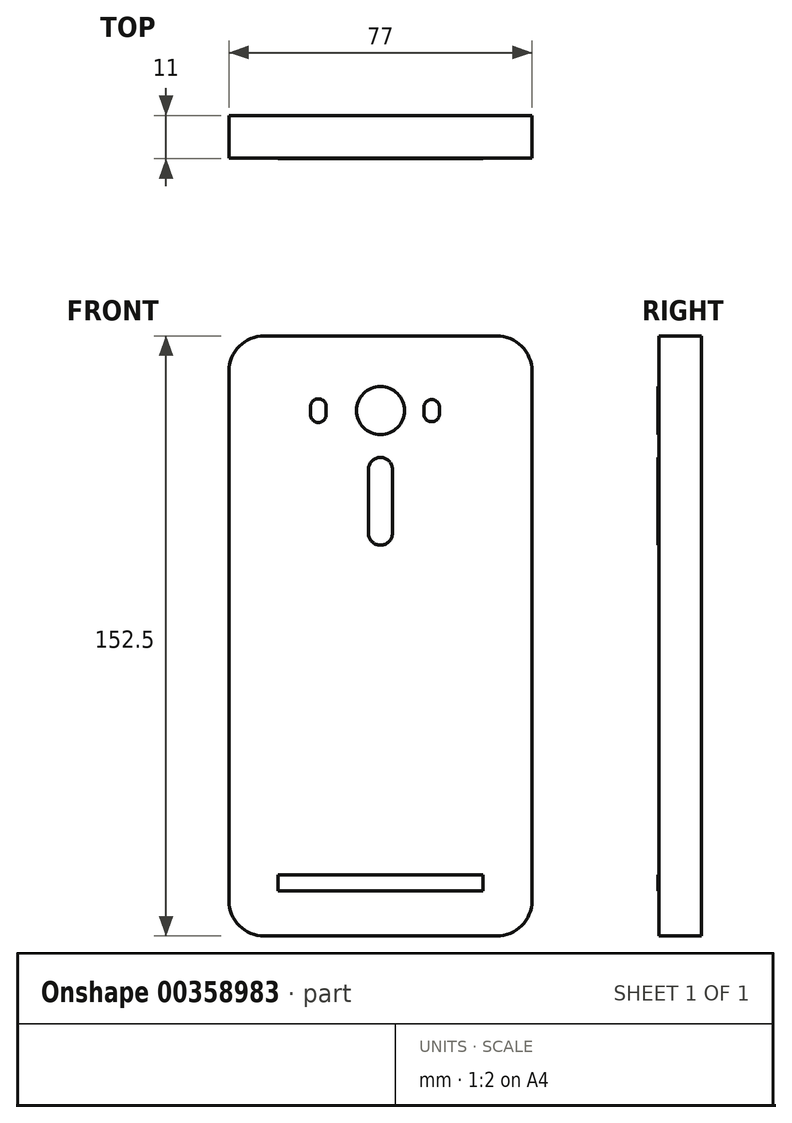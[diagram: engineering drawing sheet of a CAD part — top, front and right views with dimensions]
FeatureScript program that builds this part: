
annotation { "Feature Type Name" : "Feature", "Feature Type Description" : "" }
export const myFeature = defineFeature(function(context is Context, id is Id, definition is map)
    precondition{}
    {
        {
            var Q0;
            Q0=qCreatedBy(makeId("Front.planeOp"),FACE);
            var sketch = newSketch(context, id + "F0", { "sketchPlane" : qUnion([Q0])});
            skLineSegment(sketch, "E0.bottom", {"start": v(29.5, -76.25) * mm, "end": v(-29.5, -76.25) * mm});
            skLineSegment(sketch, "E0.top", {"start": v(29.5, 76.25) * mm, "end": v(-29.5, 76.25) * mm});
            skLineSegment(sketch, "E0.left", {"start": v(38.5, -67.25) * mm, "end": v(38.5, 67.25) * mm});
            skLineSegment(sketch, "E0.right", {"start": v(-38.5, -67.25) * mm, "end": v(-38.5, 67.25) * mm});
            skPoint(sketch, "E0.middle", {"position": v(0, 0) * mm});
            skCircle(sketch, "E1", {"center": v(0, 57.25) * mm, "radius": 6.1 * mm});
            skLineSegment(sketch, "E2.bottom", {"start": v(-15.79, 54.25) * mm, "end": v(-15.79, 54.25) * mm});
            skLineSegment(sketch, "E2.top", {"start": v(-15.79, 60.25) * mm, "end": v(-15.79, 60.25) * mm});
            skLineSegment(sketch, "E2.left", {"start": v(-13.79, 56.25) * mm, "end": v(-13.79, 58.25) * mm});
            skLineSegment(sketch, "E2.right", {"start": v(-17.79, 56.25) * mm, "end": v(-17.79, 58.25) * mm});
            skPoint(sketch, "E2.middle", {"position": v(-15.79, 57.25) * mm});
            skLineSegment(sketch, "E3.bottom", {"start": v(13.01, 54.45) * mm, "end": v(13.01, 54.45) * mm});
            skLineSegment(sketch, "E3.top", {"start": v(13.01, 60.05) * mm, "end": v(13.01, 60.05) * mm});
            skLineSegment(sketch, "E3.left", {"start": v(15.01, 56.45) * mm, "end": v(15.01, 58.05) * mm});
            skLineSegment(sketch, "E3.right", {"start": v(11.01, 56.45) * mm, "end": v(11.01, 58.05) * mm});
            skPoint(sketch, "E3.middle", {"position": v(13.01, 57.25) * mm});
            skLineSegment(sketch, "E4.bottom", {"start": v(0, 23.05) * mm, "end": v(0, 23.05) * mm});
            skLineSegment(sketch, "E4.top", {"start": v(0, 45.35) * mm, "end": v(0, 45.35) * mm});
            skLineSegment(sketch, "E4.left", {"start": v(3.05, 26.1) * mm, "end": v(3.05, 42.3) * mm});
            skLineSegment(sketch, "E4.right", {"start": v(-3.05, 26.1) * mm, "end": v(-3.05, 42.3) * mm});
            skPoint(sketch, "E4.middle", {"position": v(0, 34.2) * mm});
            skPoint(sketch, "E5.visualSharp", {"position": v(-3.05, 45.35) * mm});
            skArc(sketch, "E5.filletArc", {"start": v(0, 45.35) * mm, "mid": v(-2.16, 44.46) * mm, "end": v(-3.05, 42.3) * mm});
            skPoint(sketch, "E6.visualSharp", {"position": v(3.05, 45.35) * mm});
            skArc(sketch, "E6.filletArc", {"start": v(3.05, 42.3) * mm, "mid": v(2.16, 44.46) * mm, "end": v(0, 45.35) * mm});
            skPoint(sketch, "E7.visualSharp", {"position": v(-3.05, 23.05) * mm});
            skArc(sketch, "E7.filletArc", {"start": v(-3.05, 26.1) * mm, "mid": v(-2.16, 23.94) * mm, "end": v(0, 23.05) * mm});
            skPoint(sketch, "E8.visualSharp", {"position": v(3.05, 23.05) * mm});
            skArc(sketch, "E8.filletArc", {"start": v(0, 23.05) * mm, "mid": v(2.16, 23.94) * mm, "end": v(3.05, 26.1) * mm});
            skPoint(sketch, "E9.visualSharp", {"position": v(-17.79, 60.25) * mm});
            skArc(sketch, "E9.filletArc", {"start": v(-15.79, 60.25) * mm, "mid": v(-17.2, 59.66) * mm, "end": v(-17.79, 58.25) * mm});
            skPoint(sketch, "E10.visualSharp", {"position": v(-13.79, 60.25) * mm});
            skArc(sketch, "E10.filletArc", {"start": v(-13.79, 58.25) * mm, "mid": v(-14.37, 59.66) * mm, "end": v(-15.79, 60.25) * mm});
            skPoint(sketch, "E11.visualSharp", {"position": v(-13.79, 54.25) * mm});
            skArc(sketch, "E11.filletArc", {"start": v(-15.79, 54.25) * mm, "mid": v(-14.37, 54.84) * mm, "end": v(-13.79, 56.25) * mm});
            skPoint(sketch, "E12.visualSharp", {"position": v(-17.79, 54.25) * mm});
            skArc(sketch, "E12.filletArc", {"start": v(-17.79, 56.25) * mm, "mid": v(-17.2, 54.84) * mm, "end": v(-15.79, 54.25) * mm});
            skPoint(sketch, "E13.visualSharp", {"position": v(11.01, 60.05) * mm});
            skArc(sketch, "E13.filletArc", {"start": v(13.01, 60.05) * mm, "mid": v(11.6, 59.46) * mm, "end": v(11.01, 58.05) * mm});
            skPoint(sketch, "E14.visualSharp", {"position": v(15.01, 60.05) * mm});
            skArc(sketch, "E14.filletArc", {"start": v(15.01, 58.05) * mm, "mid": v(14.43, 59.46) * mm, "end": v(13.01, 60.05) * mm});
            skPoint(sketch, "E15.visualSharp", {"position": v(11.01, 54.45) * mm});
            skArc(sketch, "E15.filletArc", {"start": v(11.01, 56.45) * mm, "mid": v(11.6, 55.04) * mm, "end": v(13.01, 54.45) * mm});
            skPoint(sketch, "E16.visualSharp", {"position": v(15.01, 54.45) * mm});
            skArc(sketch, "E16.filletArc", {"start": v(13.01, 54.45) * mm, "mid": v(14.43, 55.04) * mm, "end": v(15.01, 56.45) * mm});
            skPoint(sketch, "E17.visualSharp", {"position": v(-38.5, 76.25) * mm});
            skArc(sketch, "E17.filletArc", {"start": v(-29.5, 76.25) * mm, "mid": v(-35.86, 73.61) * mm, "end": v(-38.5, 67.25) * mm});
            skPoint(sketch, "E18.visualSharp", {"position": v(38.5, 76.25) * mm});
            skArc(sketch, "E18.filletArc", {"start": v(38.5, 67.25) * mm, "mid": v(35.86, 73.61) * mm, "end": v(29.5, 76.25) * mm});
            skPoint(sketch, "E19.visualSharp", {"position": v(-38.5, -76.25) * mm});
            skArc(sketch, "E19.filletArc", {"start": v(-38.5, -67.25) * mm, "mid": v(-35.86, -73.61) * mm, "end": v(-29.5, -76.25) * mm});
            skPoint(sketch, "E20.visualSharp", {"position": v(38.5, -76.25) * mm});
            skArc(sketch, "E20.filletArc", {"start": v(29.5, -76.25) * mm, "mid": v(35.86, -73.61) * mm, "end": v(38.5, -67.25) * mm});
            skLineSegment(sketch, "E21.bottom", {"start": v(26.05, -64.75) * mm, "end": v(-26.05, -64.75) * mm});
            skLineSegment(sketch, "E21.top", {"start": v(26.05, -60.75) * mm, "end": v(-26.05, -60.75) * mm});
            skLineSegment(sketch, "E21.left", {"start": v(26.05, -64.75) * mm, "end": v(26.05, -60.75) * mm});
            skLineSegment(sketch, "E21.right", {"start": v(-26.05, -64.75) * mm, "end": v(-26.05, -60.75) * mm});
            skPoint(sketch, "E21.middle", {"position": v(0, -62.75) * mm});
            skSolve(sketch);
        }
        {
            var Q0;
            Q0=makeQuery(id+"F0.imprint","IMPRINT",FACE,{"disambiguationData":[TD([[makeQuery(id+"F0.imprint","IMPRINT",EDGE,{"derivedFrom":sQuery(id+"F0.wireOp",EDGE,"E0.bottom")}),-1.0]])]});
            extrude(context, id + "F1", {"entities" : qUnion([Q0]), "depth" : 10.8 * mm});
        }
        {
            var Q0;
            Q0=makeQuery(id+"F0.imprint","IMPRINT",FACE,{"disambiguationData":[TD([[makeQuery(id+"F0.imprint","IMPRINT",EDGE,{"derivedFrom":sQuery(id+"F0.wireOp",EDGE,"E1")}),1.0]])]});
            var Q1;
            Q1=makeQuery(id+"F0.imprint","IMPRINT",FACE,{"disambiguationData":[TD([[makeQuery(id+"F0.imprint","IMPRINT",EDGE,{"derivedFrom":sQuery(id+"F0.wireOp",EDGE,"E2.left")}),1.0]])]});
            var Q2;
            Q2=makeQuery(id+"F0.imprint","IMPRINT",FACE,{"disambiguationData":[TD([[makeQuery(id+"F0.imprint","IMPRINT",EDGE,{"derivedFrom":sQuery(id+"F0.wireOp",EDGE,"E3.left")}),1.0]])]});
            var Q3;
            Q3=makeQuery(id+"F0.imprint","IMPRINT",FACE,{"disambiguationData":[TD([[makeQuery(id+"F0.imprint","IMPRINT",EDGE,{"derivedFrom":sQuery(id+"F0.wireOp",EDGE,"E4.left")}),1.0]])]});
            var Q4;
            Q4=makeQuery(id+"F0.imprint","IMPRINT",FACE,{"disambiguationData":[TD([[makeQuery(id+"F0.imprint","IMPRINT",EDGE,{"derivedFrom":sQuery(id+"F0.wireOp",EDGE,"E21.bottom")}),-1.0]])]});
            extrude(context, id + "F2", {"entities" : qUnion([Q0, Q1, Q2, Q3, Q4]), "operationType" : NewBodyOperationType.ADD, "depth" : 11 * mm});
        }
    });
